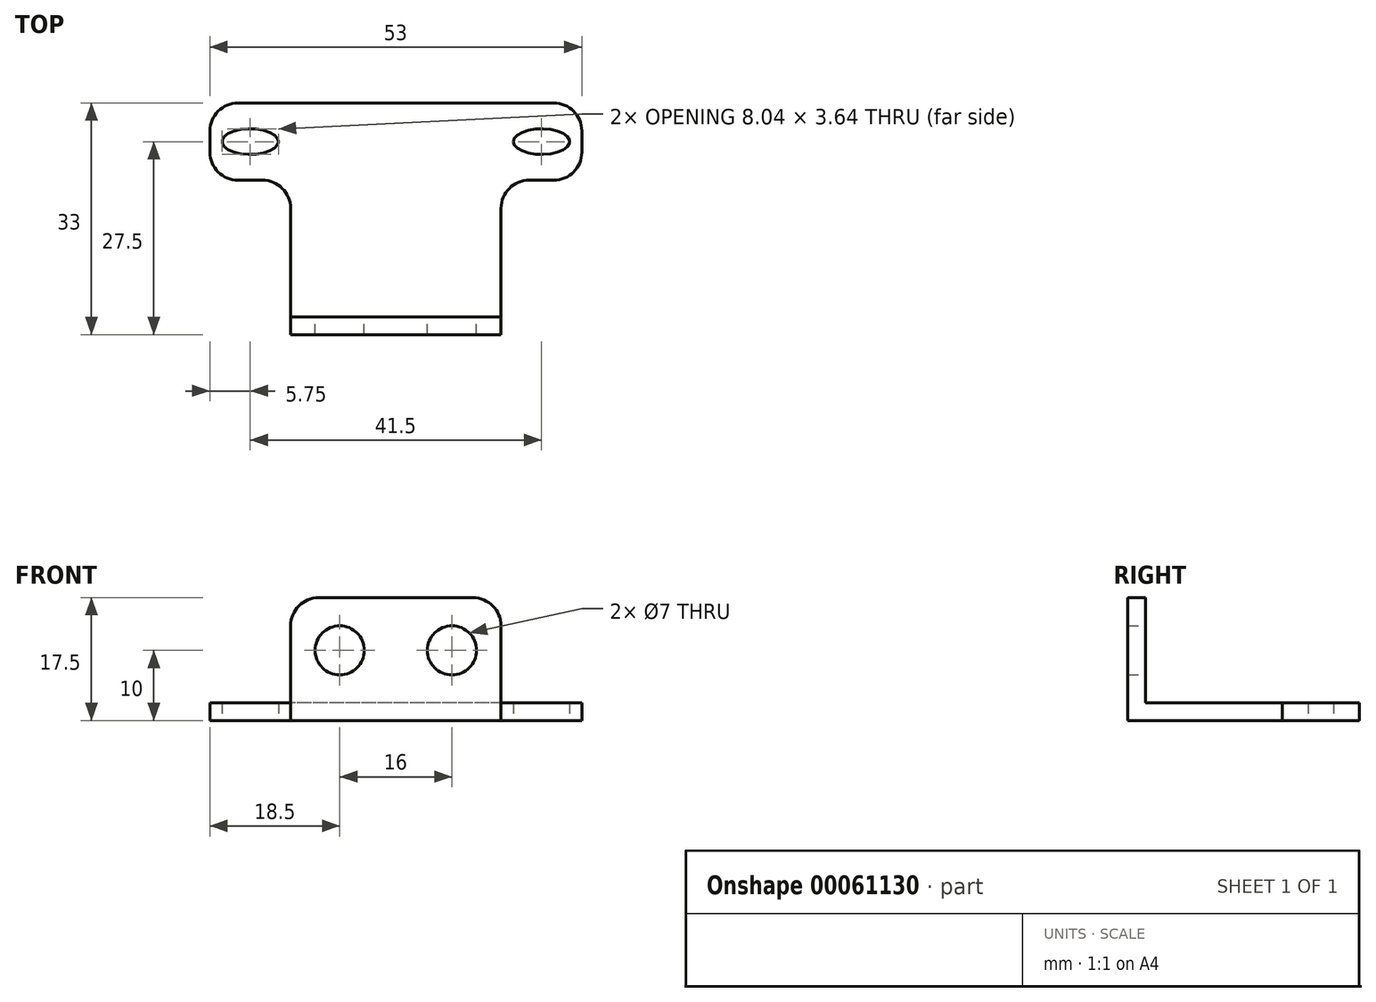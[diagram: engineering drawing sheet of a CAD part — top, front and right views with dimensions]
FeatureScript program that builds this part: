
annotation { "Feature Type Name" : "Feature", "Feature Type Description" : "" }
export const myFeature = defineFeature(function(context is Context, id is Id, definition is map)
    precondition{}
    {
        {
            var Q0;
            Q0=qCreatedBy(makeId("Top.planeOp"),FACE);
            var sketch = newSketch(context, id + "F0", { "sketchPlane" : qUnion([Q0])});
            skLineSegment(sketch, "E0.bottom", {"start": v(-11.5, 0) * mm, "end": v(-41.5, 0) * mm});
            skLineSegment(sketch, "E0.top", {"start": v(0, 33) * mm, "end": v(-53, 33) * mm});
            skLineSegment(sketch, "E0.left", {"start": v(0, 22) * mm, "end": v(0, 33) * mm});
            skLineSegment(sketch, "E0.right", {"start": v(-53, 22) * mm, "end": v(-53, 33) * mm});
            skLineSegment(sketch, "E1.top", {"start": v(-53, 22) * mm, "end": v(-41.5, 22) * mm});
            skLineSegment(sketch, "E1.right", {"start": v(-41.5, 0) * mm, "end": v(-41.5, 22) * mm});
            skLineSegment(sketch, "E2.top", {"start": v(0, 22) * mm, "end": v(-11.5, 22) * mm});
            skLineSegment(sketch, "E2.right", {"start": v(-11.5, 0) * mm, "end": v(-11.5, 22) * mm});
            skLineSegment(sketch, "E3", {"start": v(-53, 27.5) * mm, "end": v(0, 27.5) * mm, "construction": true});
            skLineSegment(sketch, "E4", {"start": v(-47.25, 22) * mm, "end": v(-47.25, 33) * mm, "construction": true});
            skLineSegment(sketch, "E5", {"start": v(-5.75, 22) * mm, "end": v(-5.75, 33) * mm, "construction": true});
            skEllipse(sketch, "E6", {"center": v(-47.25, 27.5) * mm, "majorRadius": 4.02 * mm, "minorRadius": 1.82 * mm, "majorAxis": v(1, 0)});
            skLineSegment(sketch, "E7", {"start": v(-26.5, 33) * mm, "end": v(-26.5, 21.94) * mm, "construction": true});
            skPoint(sketch, "E7.endSnap0", {"position": v(-26.5, 27.5) * mm});
            skEllipse(sketch, "E8.MirrorC", {"center": v(-5.75, 27.5) * mm, "majorRadius": 4.02 * mm, "minorRadius": 1.82 * mm, "majorAxis": v(-1, 0)});
            skSolve(sketch);
        }
        {
            var Q0;
            Q0=makeQuery(id+"F0.imprint","IMPRINT",FACE,{"disambiguationData":[TD([[makeQuery(id+"F0.imprint","IMPRINT",EDGE,{"derivedFrom":sQuery(id+"F0.wireOp",EDGE,"E0.bottom")}),-1.0]])]});
            extrude(context, id + "F1", {"entities" : qUnion([Q0]), "depth" : 2.5 * mm});
        }
        {
            var Q0;
            Q0=makeQuery(id+"F1.opExtrude","CAP_FACE",FACE,{"disambiguationData":[OSD([sQuery(id+"F0.wireOp",EDGE,"E0.bottom"),sQuery(id+"F0.wireOp",EDGE,"E0.top"),sQuery(id+"F0.wireOp",EDGE,"E0.left"),sQuery(id+"F0.wireOp",EDGE,"E0.right"),sQuery(id+"F0.wireOp",EDGE,"E1.top"),sQuery(id+"F0.wireOp",EDGE,"E1.right"),sQuery(id+"F0.wireOp",EDGE,"E2.top"),sQuery(id+"F0.wireOp",EDGE,"E2.right"),sQuery(id+"F0.wireOp",EDGE,"29332c1c-138c-4d97-a95b-52e3c1605f17"),sQuery(id+"F0.wireOp",EDGE,"253d6ffd-b237-40bb-b5be-fec14cf6fdbc")])],"isStart":false});
            var sketch = newSketch(context, id + "F2", { "sketchPlane" : qUnion([Q0])});
            skLineSegment(sketch, "E9.0", {"start": v(-11.5, 0) * mm, "end": v(-41.5, 0) * mm});
            skLineSegment(sketch, "E10.top", {"start": v(-11.5, 2.5) * mm, "end": v(-41.5, 2.5) * mm});
            skLineSegment(sketch, "E10.left", {"start": v(-11.5, 0) * mm, "end": v(-11.5, 2.5) * mm});
            skLineSegment(sketch, "E10.right", {"start": v(-41.5, 0) * mm, "end": v(-41.5, 2.5) * mm});
            skSolve(sketch);
        }
        {
            var Q0;
            Q0=makeQuery(id+"F2.imprint","IMPRINT",FACE,{"disambiguationData":[TD([[makeQuery(id+"F2.imprint","IMPRINT",EDGE,{"derivedFrom":sQuery(id+"F2.wireOp",EDGE,"E9.0")}),-1.0]])]});
            extrude(context, id + "F3", {"entities" : qUnion([Q0]), "operationType" : NewBodyOperationType.ADD, "depth" : 15 * mm});
        }
        {
            var Q0;
            Q0=makeQuery(id+"F3.opExtrude","SWEPT_FACE",FACE,{"disambiguationData":[OSD([sQuery(id+"F2.wireOp",EDGE,"E10.top")])]});
            var sketch = newSketch(context, id + "F4", { "sketchPlane" : qUnion([Q0])});
            skLineSegment(sketch, "E11", {"start": v(11.5, 10) * mm, "end": v(41.5, 10) * mm, "construction": true});
            skCircle(sketch, "E12", {"center": v(18.5, 10) * mm, "radius": 3.5 * mm});
            skLineSegment(sketch, "E13", {"start": v(26.5, 17.5) * mm, "end": v(26.5, 2.5) * mm, "construction": true});
            skCircle(sketch, "E14", {"center": v(34.5, 10) * mm, "radius": 3.5 * mm});
            skSolve(sketch);
        }
        {
            var Q0;
            Q0=makeQuery(id+"F4.imprint","IMPRINT",FACE,{"disambiguationData":[TD([[makeQuery(id+"F4.imprint","IMPRINT",EDGE,{"derivedFrom":sQuery(id+"F4.wireOp",EDGE,"E12")}),1.0]])]});
            var Q1;
            Q1=makeQuery(id+"F4.imprint","IMPRINT",FACE,{"disambiguationData":[TD([[makeQuery(id+"F4.imprint","IMPRINT",EDGE,{"derivedFrom":sQuery(id+"F4.wireOp",EDGE,"E14")}),1.0]])]});
            extrude(context, id + "F5", {"entities" : qUnion([Q0, Q1]), "operationType" : NewBodyOperationType.REMOVE, "endBound" : BoundingType.THROUGH_ALL, "oppositeDirection" : true, "depth" : 25 * mm});
        }
        {
            var Q0;
            Q0=makeQuery(id+"F1.opExtrude","SWEPT_EDGE",EDGE,{"disambiguationData":[OSD([sQuery(id+"F0.wireOp",EDGE,"E0.top"),sQuery(id+"F0.wireOp",EDGE,"E0.left")])]});
            var Q1;
            Q1=makeQuery(id+"F1.opExtrude","SWEPT_EDGE",EDGE,{"disambiguationData":[OSD([sQuery(id+"F0.wireOp",EDGE,"E0.top"),sQuery(id+"F0.wireOp",EDGE,"E0.right")])]});
            var Q2;
            Q2=makeQuery(id+"F1.opExtrude","SWEPT_EDGE",EDGE,{"disambiguationData":[OSD([sQuery(id+"F0.wireOp",EDGE,"E0.right"),sQuery(id+"F0.wireOp",EDGE,"E1.top")])]});
            var Q3;
            Q3=makeQuery(id+"F1.opExtrude","SWEPT_EDGE",EDGE,{"disambiguationData":[OSD([sQuery(id+"F0.wireOp",EDGE,"E1.top"),sQuery(id+"F0.wireOp",EDGE,"E1.right")])]});
            var Q4;
            Q4=makeQuery(id+"F1.opExtrude","SWEPT_EDGE",EDGE,{"disambiguationData":[OSD([sQuery(id+"F0.wireOp",EDGE,"E2.top"),sQuery(id+"F0.wireOp",EDGE,"E2.right")])]});
            var Q5;
            Q5=makeQuery(id+"F1.opExtrude","SWEPT_EDGE",EDGE,{"disambiguationData":[OSD([sQuery(id+"F0.wireOp",EDGE,"E0.left"),sQuery(id+"F0.wireOp",EDGE,"E2.top")])]});
            var Q6;
            Q6=makeQuery(id+"F3.opExtrude","CAP_EDGE",EDGE,{"disambiguationData":[OSD([sQuery(id+"F2.wireOp",EDGE,"E10.top")])],"isStart":true});
            var Q7;
            Q7=makeQuery(id+"F3.opExtrude","CAP_EDGE",EDGE,{"disambiguationData":[OSD([sQuery(id+"F2.wireOp",EDGE,"E10.left")])],"isStart":false});
            var Q8;
            Q8=makeQuery(id+"F3.opExtrude","CAP_EDGE",EDGE,{"disambiguationData":[OSD([sQuery(id+"F2.wireOp",EDGE,"E10.right")])],"isStart":false});
            fillet(context, id + "F6", {"entities" : qUnion([Q0, Q1, Q2, Q3, Q4, Q5, Q6, Q7, Q8]), "radius" : 4 * mm, "tangentPropagation" : true, "allowEdgeOverflow" : false});
        }
    });
